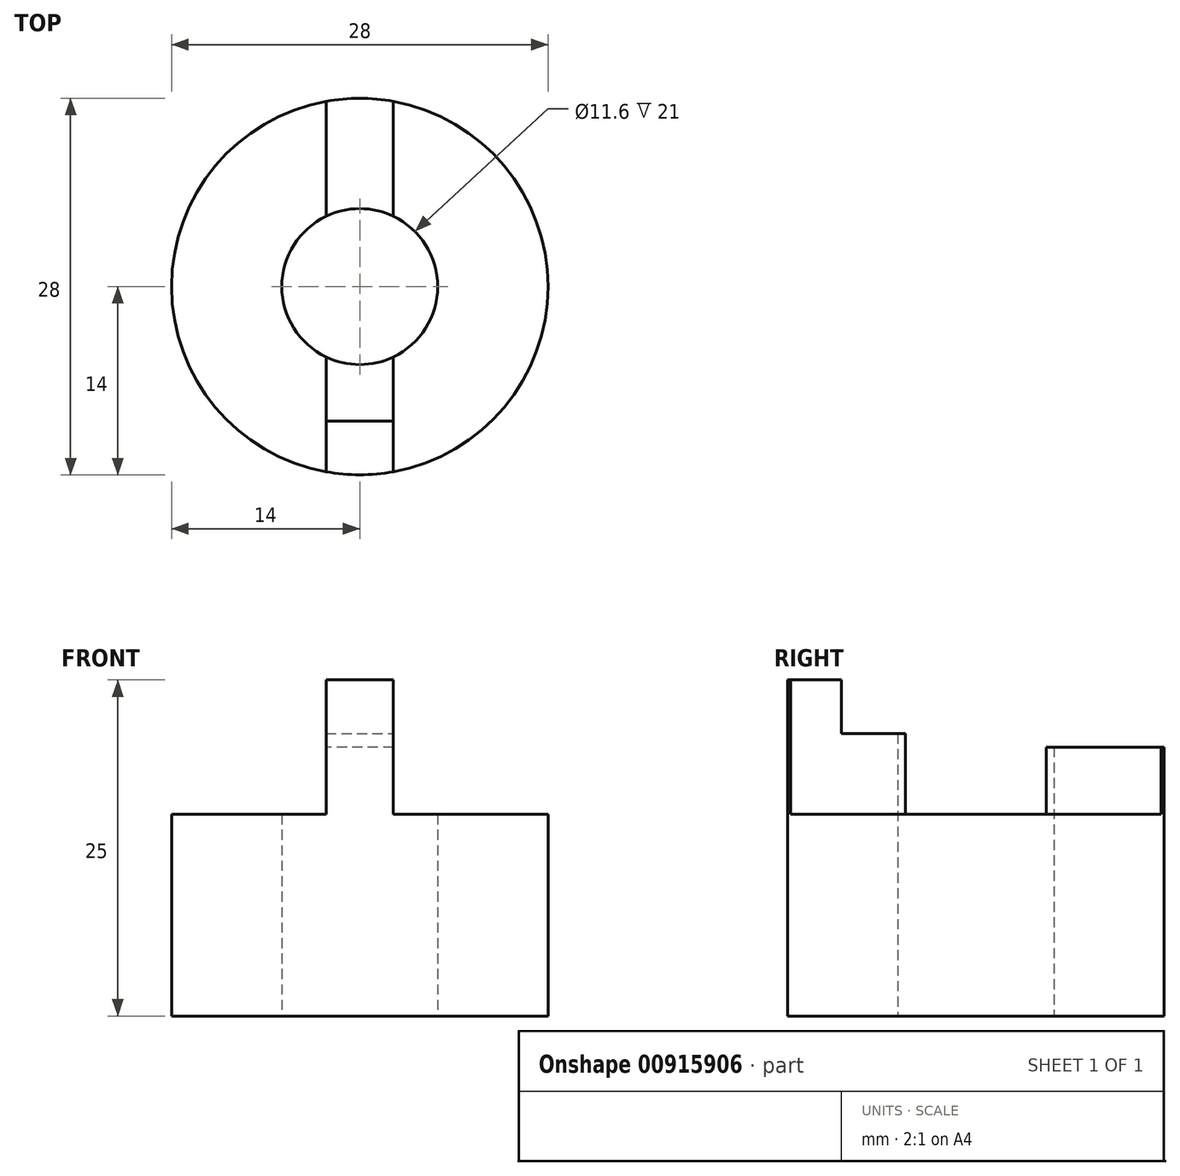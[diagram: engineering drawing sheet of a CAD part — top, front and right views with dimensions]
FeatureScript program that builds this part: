
annotation { "Feature Type Name" : "Feature", "Feature Type Description" : "" }
export const myFeature = defineFeature(function(context is Context, id is Id, definition is map)
    precondition{}
    {
        {
            var Q0;
            Q0=qCreatedBy(makeId("Top.planeOp"),FACE);
            var sketch = newSketch(context, id + "F0", { "sketchPlane" : qUnion([Q0])});
            skCircle(sketch, "E0", {"center": v(0, 0) * mm, "radius": 14 * mm});
            skSolve(sketch);
        }
        {
            var Q0;
            Q0=makeQuery(id+"F0.imprint","IMPRINT",FACE,{"disambiguationData":[TD([[makeQuery(id+"F0.imprint","IMPRINT",EDGE,{"derivedFrom":sQuery(id+"F0.wireOp",EDGE,"E0")}),1.0]])]});
            extrude(context, id + "F1", {"entities" : qUnion([Q0]), "depth" : 20 * mm, "offsetDistance" : 25 * mm});
        }
        {
            var Q0;
            Q0=makeQuery(id+"F1.opExtrude","CAP_FACE",FACE,{"disambiguationData":[OSD([sQuery(id+"F0.wireOp",EDGE,"E0")])],"isStart":true});
            var sketch = newSketch(context, id + "F2", { "sketchPlane" : qUnion([Q0])});
            skCircle(sketch, "E1", {"center": v(0, 0) * mm, "radius": 5.8 * mm});
            skSolve(sketch);
        }
        {
            var Q0;
            Q0=makeQuery(id+"F2.imprint","IMPRINT",FACE,{"disambiguationData":[TD([[makeQuery(id+"F2.imprint","IMPRINT",EDGE,{"derivedFrom":sQuery(id+"F2.wireOp",EDGE,"E1")}),1.0]])]});
            extrude(context, id + "F3", {"entities" : qUnion([Q0]), "operationType" : NewBodyOperationType.REMOVE, "endBound" : BoundingType.THROUGH_ALL, "oppositeDirection" : true, "depth" : 25 * mm, "offsetDistance" : 25 * mm});
        }
        {
            var Q0;
            Q0=makeQuery(id+"F1.opExtrude","CAP_FACE",FACE,{"disambiguationData":[OSD([sQuery(id+"F0.wireOp",EDGE,"E0")])],"isStart":false});
            var sketch = newSketch(context, id + "F4", { "sketchPlane" : qUnion([Q0])});
            skLineSegment(sketch, "E2", {"start": v(-14, 0) * mm, "end": v(14, 0) * mm, "construction": true});
            skLineSegment(sketch, "E3", {"start": v(0, 14) * mm, "end": v(0, -14) * mm, "construction": true});
            skLineSegment(sketch, "E4", {"start": v(2.5, 13.77) * mm, "end": v(2.5, -13.77) * mm});
            skLineSegment(sketch, "E5", {"start": v(-2.5, 13.77) * mm, "end": v(-2.5, -13.77) * mm});
            skSolve(sketch);
        }
        {
            var Q0;
            {var subQ0=sQuery(id+"F4.wireOp",EDGE,"E5");var subQ1=sQuery(id+"F0.wireOp",EDGE,"E0");var subQ2=makeQuery(id+"F1.opExtrude","CAP_EDGE",EDGE,{"disambiguationData":[OSD([subQ1])],"isStart":false});var subQ3=makeQuery(id+"F4.imprint","INTERSECT",VERTEX,{"disambiguationData":[OD(0.0)],"derivedFrom":[subQ2,subQ0]});Q0=makeQuery(id+"F4.imprint","IMPRINT",FACE,{"disambiguationData":[TD([[makeQuery(id+"F4.imprint","IMPRINT",EDGE,{"disambiguationData":[TD([[subQ3,-1.0]])],"derivedFrom":subQ2}),1.0]])]});}
            extrude(context, id + "F5", {"entities" : qUnion([Q0]), "operationType" : NewBodyOperationType.REMOVE, "oppositeDirection" : true, "depth" : 5 * mm, "offsetDistance" : 25 * mm});
        }
        {
            var Q0;
            {var subQ0=sQuery(id+"F4.wireOp",EDGE,"E4");var subQ1=sQuery(id+"F0.wireOp",EDGE,"E0");var subQ2=makeQuery(id+"F1.opExtrude","CAP_EDGE",EDGE,{"disambiguationData":[OSD([subQ1])],"isStart":false});var subQ3=makeQuery(id+"F4.imprint","INTERSECT",VERTEX,{"disambiguationData":[OD(0.0)],"derivedFrom":[subQ2,subQ0]});Q0=makeQuery(id+"F4.imprint","IMPRINT",FACE,{"disambiguationData":[TD([[makeQuery(id+"F4.imprint","IMPRINT",EDGE,{"disambiguationData":[TD([[subQ3,1.0]])],"derivedFrom":subQ2}),1.0]])]});}
            extrude(context, id + "F6", {"entities" : qUnion([Q0]), "operationType" : NewBodyOperationType.REMOVE, "oppositeDirection" : true, "depth" : 5 * mm, "offsetDistance" : 25 * mm});
        }
        {
            var Q0;
            {var subQ0=sQuery(id+"F4.wireOp",EDGE,"E4");var subQ1=sQuery(id+"F0.wireOp",EDGE,"E0");var subQ2=makeQuery(id+"F1.opExtrude","CAP_EDGE",EDGE,{"disambiguationData":[OSD([subQ1])],"isStart":false});var subQ3=makeQuery(id+"F4.imprint","INTERSECT",VERTEX,{"disambiguationData":[OD(1.0)],"derivedFrom":[subQ2,subQ0]});Q0=makeQuery(id+"F4.imprint","IMPRINT",FACE,{"disambiguationData":[TD([[makeQuery(id+"F4.imprint","IMPRINT",EDGE,{"disambiguationData":[TD([[subQ3,1.0]])],"derivedFrom":subQ2}),1.0]])]});}
            extrude(context, id + "F7", {"entities" : qUnion([Q0]), "operationType" : NewBodyOperationType.ADD, "depth" : 5 * mm, "offsetDistance" : 25 * mm});
        }
        {
            var Q0;
            Q0=makeQuery(id+"F7.opExtrude","CAP_FACE",FACE,{"disambiguationData":[OSD([sQuery(id+"F0.wireOp",EDGE,"E0"),sQuery(id+"F2.wireOp",EDGE,"E1"),sQuery(id+"F4.wireOp",EDGE,"E4"),sQuery(id+"F4.wireOp",EDGE,"E5")])],"isStart":false});
            var sketch = newSketch(context, id + "F8", { "sketchPlane" : qUnion([Q0])});
            skLineSegment(sketch, "E6", {"start": v(-2.5, -10) * mm, "end": v(2.5, -10) * mm});
            skSolve(sketch);
        }
        {
            var Q0;
            {var subQ0=sQuery(id+"F8.wireOp",EDGE,"E6");Q0=makeQuery(id+"F8.imprint","IMPRINT",FACE,{"disambiguationData":[TD([[makeQuery(id+"F8.imprint","IMPRINT",EDGE,{"derivedFrom":subQ0}),1.0]])]});}
            extrude(context, id + "F9", {"entities" : qUnion([Q0]), "operationType" : NewBodyOperationType.REMOVE, "oppositeDirection" : true, "depth" : 4 * mm, "offsetDistance" : 25 * mm});
        }
    });
